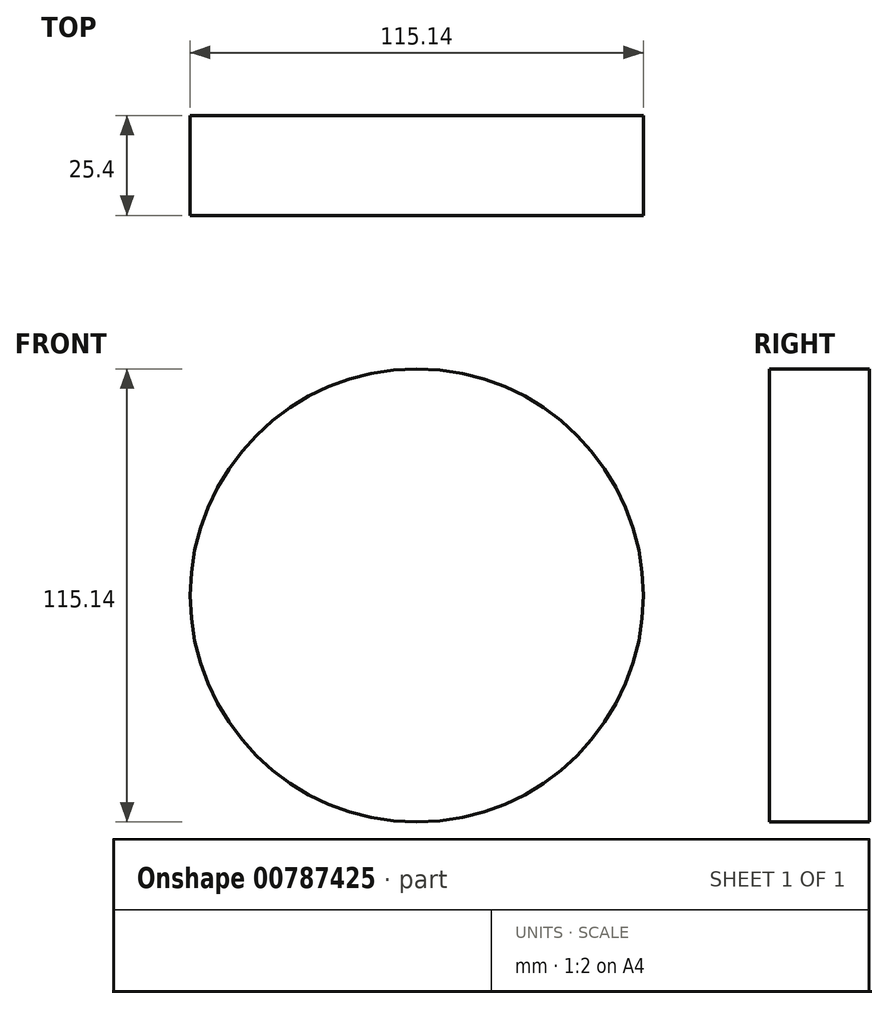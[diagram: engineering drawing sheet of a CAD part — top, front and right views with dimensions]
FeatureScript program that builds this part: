
annotation { "Feature Type Name" : "Feature", "Feature Type Description" : "" }
export const myFeature = defineFeature(function(context is Context, id is Id, definition is map)
    precondition{}
    {
        {
            var Q0;
            Q0=qCreatedBy(makeId("Front.planeOp"),FACE);
            var sketch = newSketch(context, id + "F0", { "sketchPlane" : qUnion([Q0])});
            skCircle(sketch, "E0", {"center": v(0, 0) * mm, "radius": 57.57 * mm});
            skSolve(sketch);
        }
        {
            var Q0;
            Q0=makeQuery(id+"F0.imprint","IMPRINT",FACE,{"disambiguationData":[TD([[makeQuery(id+"F0.imprint","IMPRINT",EDGE,{"derivedFrom":sQuery(id+"F0.wireOp",EDGE,"E0")}),1.0]])]});
            extrude(context, id + "F1", {"entities" : qUnion([Q0]), "depth" : 25.4 * mm, "offsetDistance" : 25.4 * mm});
        }
    });
